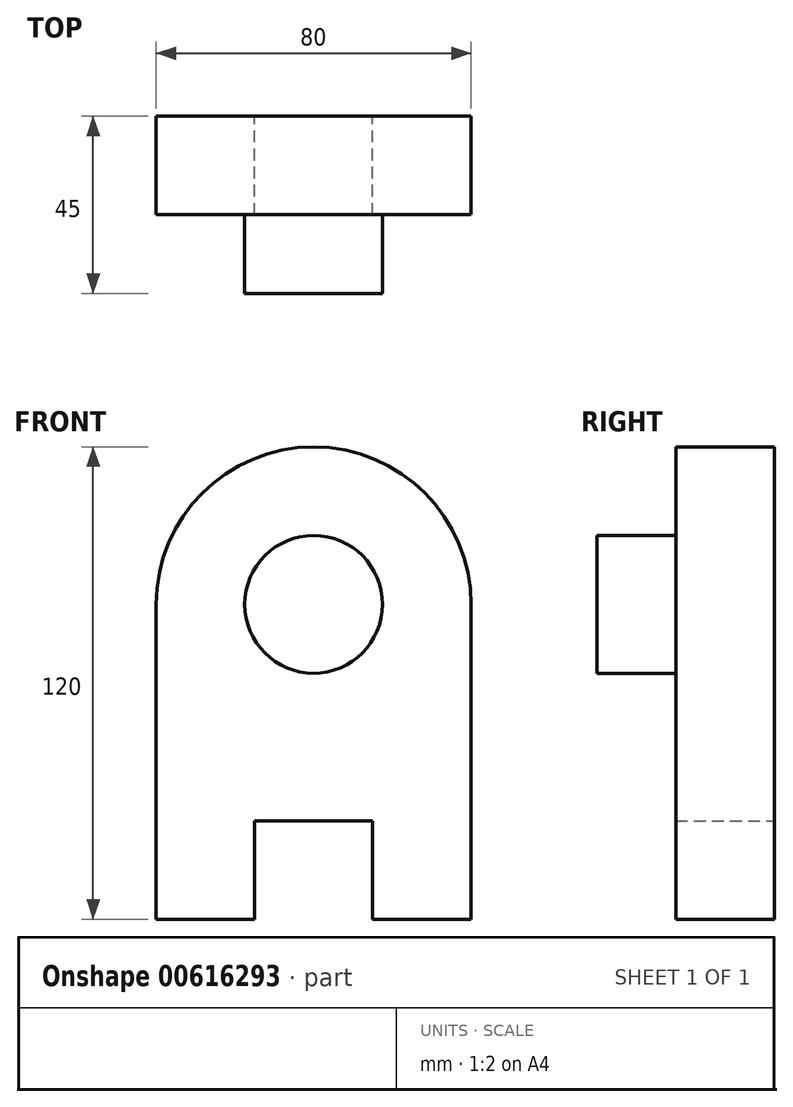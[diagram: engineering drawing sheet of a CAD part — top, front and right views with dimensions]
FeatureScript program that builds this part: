
annotation { "Feature Type Name" : "Feature", "Feature Type Description" : "" }
export const myFeature = defineFeature(function(context is Context, id is Id, definition is map)
    precondition{}
    {
        {
            var Q0;
            Q0=qCreatedBy(makeId("Front.planeOp"),FACE);
            var sketch = newSketch(context, id + "F0", { "sketchPlane" : qUnion([Q0])});
            skArc(sketch, "E0", {"start": v(40, 0) * mm, "mid": v(0, 40) * mm, "end": v(-40, 0) * mm});
            skCircle(sketch, "E1", {"center": v(0, 0) * mm, "radius": 17.5 * mm});
            skLineSegment(sketch, "E2", {"start": v(-40, 0) * mm, "end": v(-40, -80) * mm});
            skLineSegment(sketch, "E3", {"start": v(40, 0) * mm, "end": v(40, -80) * mm});
            skLineSegment(sketch, "E4", {"start": v(-40, -80) * mm, "end": v(-15, -80) * mm});
            skLineSegment(sketch, "E5", {"start": v(40, -80) * mm, "end": v(15, -80) * mm});
            skLineSegment(sketch, "E6", {"start": v(-15, -80) * mm, "end": v(-15, -55) * mm});
            skLineSegment(sketch, "E7", {"start": v(15, -80) * mm, "end": v(15, -55) * mm});
            skLineSegment(sketch, "E8", {"start": v(-15, -55) * mm, "end": v(15, -55) * mm});
            skLineSegment(sketch, "E9", {"start": v(156.26, 71.54) * mm, "end": v(156.26, 78.14) * mm});
            skSolve(sketch);
        }
        {
            var Q0;
            Q0=makeQuery(id+"F0.imprint","IMPRINT",FACE,{"disambiguationData":[TD([[makeQuery(id+"F0.imprint","IMPRINT",EDGE,{"derivedFrom":sQuery(id+"F0.wireOp",EDGE,"E1")}),1.0]])]});
            extrude(context, id + "F1", {"entities" : qUnion([Q0]), "depth" : 45 * mm, "offsetDistance" : 25 * mm});
        }
        {
            var Q0;
            Q0 = qSketchRegion(id + "F0", true);
            extrude(context, id + "F2", {"entities" : qUnion([Q0]), "operationType" : NewBodyOperationType.ADD, "depth" : 25 * mm, "offsetDistance" : 25 * mm});
        }
    });
